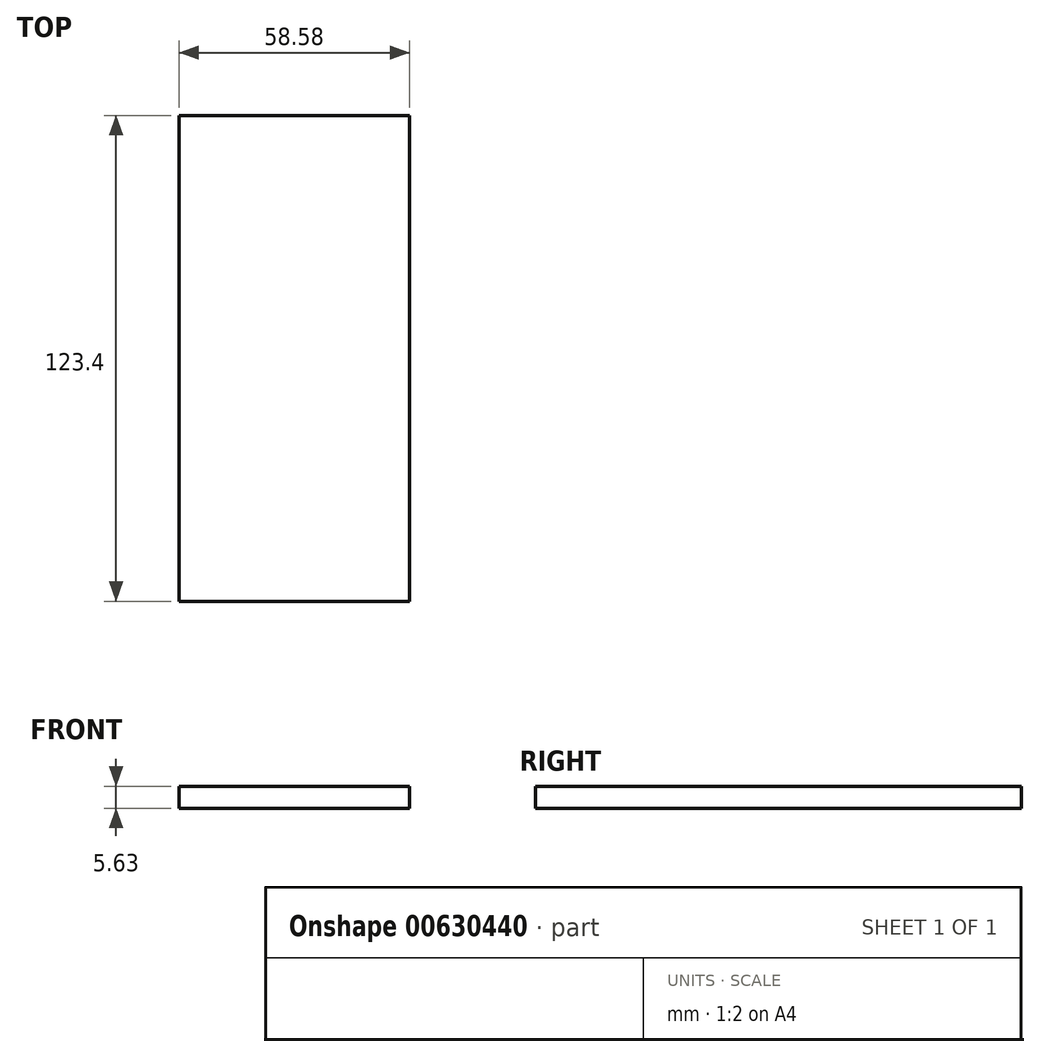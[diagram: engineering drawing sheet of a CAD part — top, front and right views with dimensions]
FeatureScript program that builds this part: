
annotation { "Feature Type Name" : "Feature", "Feature Type Description" : "" }
export const myFeature = defineFeature(function(context is Context, id is Id, definition is map)
    precondition{}
    {
        {
            var Q0;
            Q0=qCreatedBy(makeId("Top.planeOp"),FACE);
            var sketch = newSketch(context, id + "F0", { "sketchPlane" : qUnion([Q0])});
            skLineSegment(sketch, "E0.bottom", {"start": v(29.29, 61.7) * mm, "end": v(-29.28, 61.7) * mm});
            skLineSegment(sketch, "E0.top", {"start": v(29.28, -61.7) * mm, "end": v(-29.29, -61.7) * mm});
            skLineSegment(sketch, "E0.left", {"start": v(29.29, 61.7) * mm, "end": v(29.28, -61.7) * mm});
            skLineSegment(sketch, "E0.right", {"start": v(-29.28, 61.7) * mm, "end": v(-29.29, -61.7) * mm});
            skPoint(sketch, "E0.middle", {"position": v(0, 0) * mm});
            skSolve(sketch);
        }
        {
            var Q0;
            Q0 = qSketchRegion(id + "F0", true);
            extrude(context, id + "F1", {"entities" : qUnion([Q0]), "depth" : 5.63 * mm, "offsetDistance" : 25 * mm});
        }
    });
